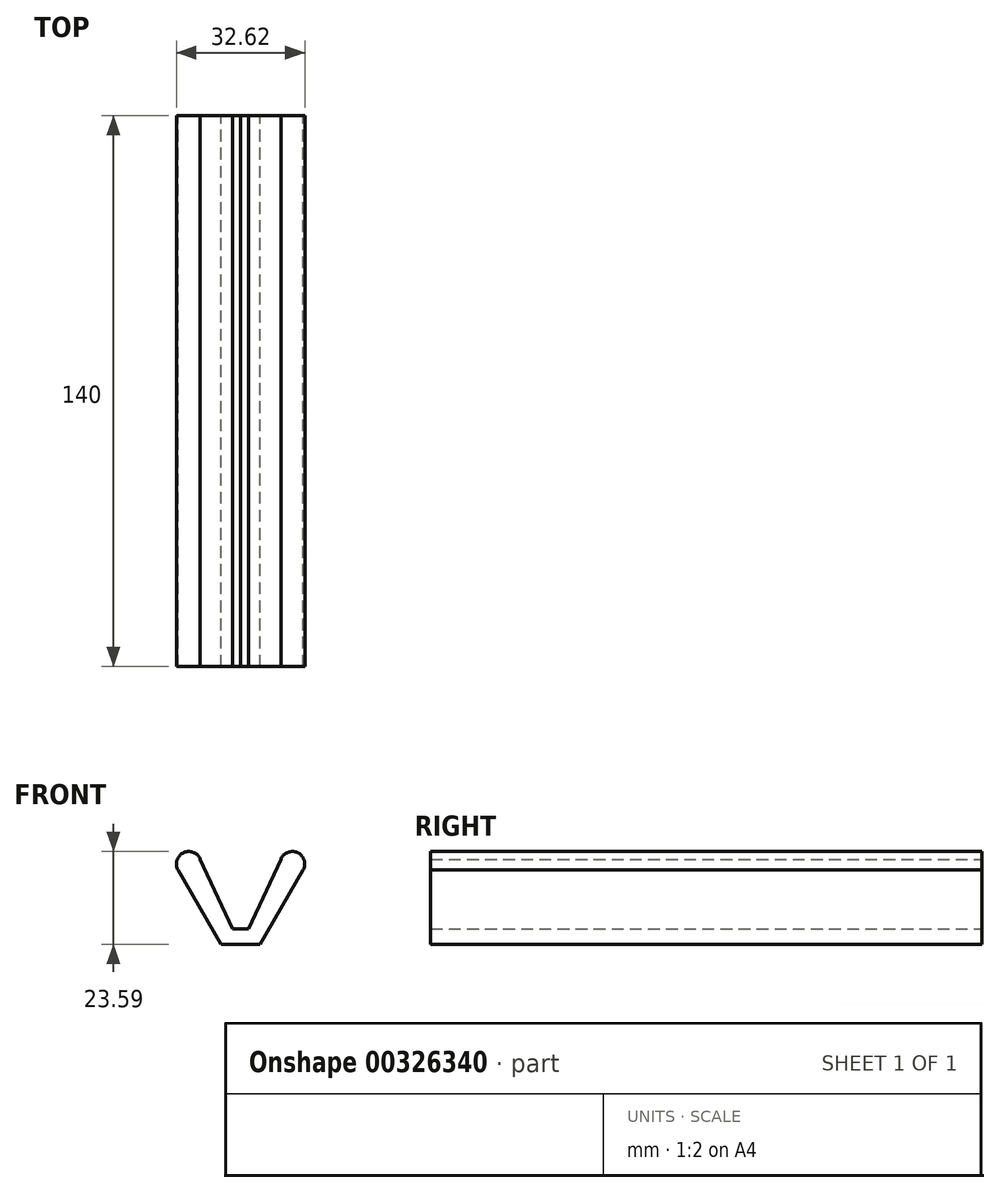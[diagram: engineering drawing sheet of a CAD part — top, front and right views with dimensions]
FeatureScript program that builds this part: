
annotation { "Feature Type Name" : "Feature", "Feature Type Description" : "" }
export const myFeature = defineFeature(function(context is Context, id is Id, definition is map)
    precondition{}
    {
        {
            var Q0;
            Q0=qCreatedBy(makeId("Front.planeOp"),FACE);
            var sketch = newSketch(context, id + "F0", { "sketchPlane" : qUnion([Q0])});
            skLineSegment(sketch, "E0", {"start": v(0, 0) * mm, "end": v(5, 0) * mm});
            skPoint(sketch, "E1", {"position": v(0, 0) * mm});
            skLineSegment(sketch, "E2", {"start": v(5, 0) * mm, "end": v(17.5, 21.65) * mm});
            skLineSegment(sketch, "E3", {"start": v(0, 0) * mm, "end": v(0, 4) * mm, "construction": true});
            skLineSegment(sketch, "E4", {"start": v(2, 3.98) * mm, "end": v(14.17, 30.09) * mm});
            skLineSegment(sketch, "E5", {"start": v(17.5, 21.65) * mm, "end": v(-1.89, 21.65) * mm, "construction": true});
            skLineSegment(sketch, "E6", {"start": v(0, 4) * mm, "end": v(2, 3.98) * mm});
            skArc(sketch, "E7", {"start": v(15.9, 18.89) * mm, "mid": v(14.54, 23.27) * mm, "end": v(10.24, 21.65) * mm});
            skLineSegment(sketch, "E8.MirrorCS", {"start": v(-2, 3.98) * mm, "end": v(-14.17, 30.09) * mm});
            skArc(sketch, "E9.MirrorCS", {"start": v(-15.9, 18.89) * mm, "mid": v(-14.54, 23.27) * mm, "end": v(-10.24, 21.65) * mm});
            skLineSegment(sketch, "E10.MirrorCS", {"start": v(-5, 0) * mm, "end": v(-17.5, 21.65) * mm});
            skLineSegment(sketch, "E11.MirrorCS", {"start": v(0, 0) * mm, "end": v(-5, 0) * mm});
            skLineSegment(sketch, "E12.MirrorCS", {"start": v(0, 4) * mm, "end": v(-2, 3.98) * mm});
            skSolve(sketch);
        }
        {
            var Q0;
            Q0 = qSketchRegion(id + "F0", true);
            extrude(context, id + "F1", {"entities" : qUnion([Q0]), "depth" : 140 * mm});
        }
    });
